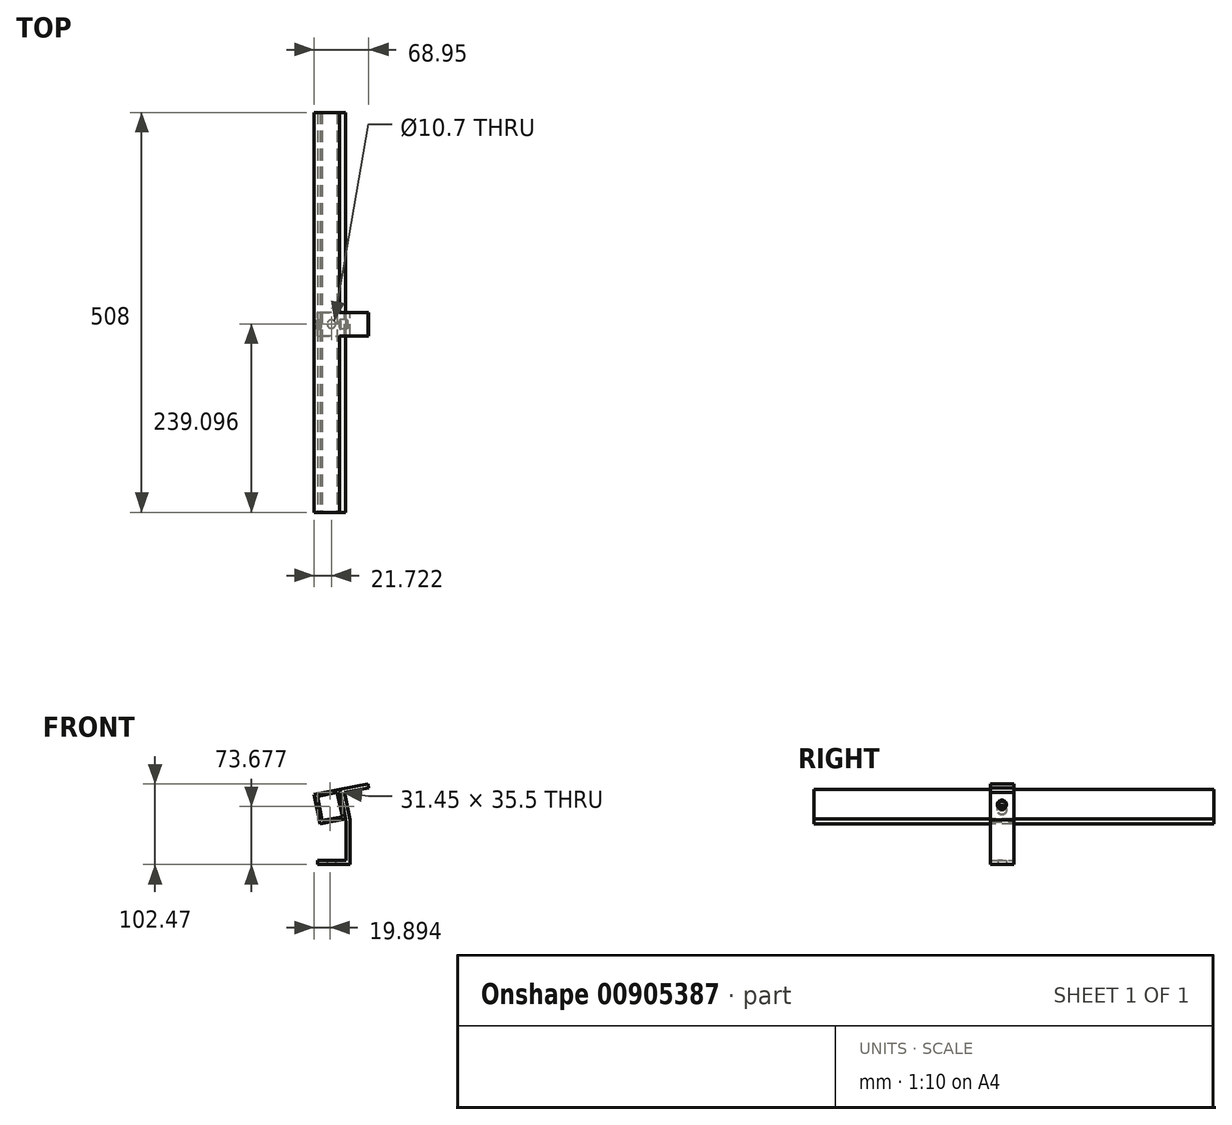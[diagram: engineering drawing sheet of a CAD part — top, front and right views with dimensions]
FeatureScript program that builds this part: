
annotation { "Feature Type Name" : "Feature", "Feature Type Description" : "" }
export const myFeature = defineFeature(function(context is Context, id is Id, definition is map)
    precondition{}
    {
        {
            var Q0;
            Q0=qCreatedBy(makeId("Front.planeOp"),FACE);
            var sketch = newSketch(context, id + "F0", { "sketchPlane" : qUnion([Q0])});
            skLineSegment(sketch, "E0", {"start": v(0, 0) * mm, "end": v(0, 5) * mm});
            skLineSegment(sketch, "E1", {"start": v(0, 5) * mm, "end": v(36, 5) * mm});
            skLineSegment(sketch, "E2", {"start": v(36, 5) * mm, "end": v(36, 54.43) * mm});
            skLineSegment(sketch, "E3", {"start": v(41, 56.52) * mm, "end": v(41, 0) * mm});
            skLineSegment(sketch, "E4", {"start": v(41, 0) * mm, "end": v(0, 0) * mm});
            skLineSegment(sketch, "E5", {"start": v(41, 56.52) * mm, "end": v(34.23, 91.68) * mm});
            skLineSegment(sketch, "E6", {"start": v(34.23, 91.68) * mm, "end": v(64.78, 97.56) * mm});
            skLineSegment(sketch, "E7", {"start": v(64.78, 97.56) * mm, "end": v(63.83, 102.47) * mm});
            skLineSegment(sketch, "E8", {"start": v(63.83, 102.47) * mm, "end": v(28.07, 95.59) * mm});
            skLineSegment(sketch, "E9", {"start": v(28.07, 95.59) * mm, "end": v(36, 54.43) * mm});
            skSolve(sketch);
        }
        {
            var Q0;
            Q0=makeQuery(id+"F0.imprint","IMPRINT",FACE,{"disambiguationData":[TD([[makeQuery(id+"F0.imprint","IMPRINT",EDGE,{"derivedFrom":sQuery(id+"F0.wireOp",EDGE,"E0")}),-1.0]])]});
            extrude(context, id + "F1", {"entities" : qUnion([Q0]), "depth" : 30 * mm, "offsetDistance" : 25.4 * mm});
        }
        {
            var Q0;
            Q0=makeQuery(id+"F1.opExtrude","SWEPT_FACE",FACE,{"disambiguationData":[OSD([sQuery(id+"F0.wireOp",EDGE,"E9")])]});
            var sketch = newSketch(context, id + "F2", { "sketchPlane" : qUnion([Q0])});
            skCircle(sketch, "E10", {"center": v(15.32, 67.61) * mm, "radius": 5.9 * mm});
            skLineSegment(sketch, "E11", {"start": v(15, 88.55) * mm, "end": v(15.64, 46.64) * mm, "construction": true});
            skLineSegment(sketch, "E12", {"start": v(-0.72, 67.6) * mm, "end": v(31.06, 67.6) * mm, "construction": true});
            skPoint(sketch, "E12.startSnap0", {"position": v(0, 67.6) * mm});
            skSolve(sketch);
        }
        {
            var Q0;
            Q0=makeQuery(id+"F2.imprint","IMPRINT",FACE,{"disambiguationData":[TD([[makeQuery(id+"F2.imprint","IMPRINT",EDGE,{"derivedFrom":sQuery(id+"F2.wireOp",EDGE,"E10")}),1.0]])]});
            extrude(context, id + "F3", {"entities" : qUnion([Q0]), "operationType" : NewBodyOperationType.REMOVE, "endBound" : BoundingType.THROUGH_ALL, "oppositeDirection" : true, "depth" : 25.4 * mm, "offsetDistance" : 25.4 * mm});
        }
        {
            var Q0;
            Q0=makeQuery(id+"F1.opExtrude","CAP_FACE",FACE,{"disambiguationData":[OSD([sQuery(id+"F0.wireOp",EDGE,"E0"),sQuery(id+"F0.wireOp",EDGE,"E1"),sQuery(id+"F0.wireOp",EDGE,"E2"),sQuery(id+"F0.wireOp",EDGE,"E3"),sQuery(id+"F0.wireOp",EDGE,"E4"),sQuery(id+"F0.wireOp",EDGE,"E5"),sQuery(id+"F0.wireOp",EDGE,"E6"),sQuery(id+"F0.wireOp",EDGE,"E7"),sQuery(id+"F0.wireOp",EDGE,"E8"),sQuery(id+"F0.wireOp",EDGE,"E9")])],"isStart":true});
            var sketch = newSketch(context, id + "F4", { "sketchPlane" : qUnion([Q0])});
            skLineSegment(sketch, "E13", {"start": v(-28.07, 95.59) * mm, "end": v(4.17, 89.38) * mm});
            skLineSegment(sketch, "E14", {"start": v(4.17, 89.38) * mm, "end": v(-3.12, 51.53) * mm});
            skLineSegment(sketch, "E15", {"start": v(-3.12, 51.53) * mm, "end": v(-35.36, 57.74) * mm});
            skLineSegment(sketch, "E16", {"start": v(-24.86, 91.43) * mm, "end": v(0, 86.64) * mm});
            skLineSegment(sketch, "E17", {"start": v(0, 86.64) * mm, "end": v(-5.91, 55.93) * mm});
            skLineSegment(sketch, "E18", {"start": v(-5.91, 55.93) * mm, "end": v(-31.45, 60.84) * mm});
            skLineSegment(sketch, "E19", {"start": v(-31.45, 60.84) * mm, "end": v(-24.86, 91.43) * mm});
            skSolve(sketch);
        }
        {
            var Q0;
            {var subQ1=sQuery(id+"F4.wireOp",EDGE,"E13");Q0=makeQuery(id+"F4.imprint","IMPRINT",FACE,{"disambiguationData":[TD([[makeQuery(id+"F4.imprint","IMPRINT",EDGE,{"derivedFrom":subQ1}),-1.0]])]});}
            extrude(context, id + "F5", {"entities" : qUnion([Q0]), "operationType" : NewBodyOperationType.ADD, "endBound" : BoundingType.SYMMETRIC, "depth" : 508 * mm, "offsetDistance" : 25.4 * mm});
        }
        {
            var Q0;
            Q0=makeQuery(id+"F1.opExtrude","SWEPT_FACE",FACE,{"disambiguationData":[OSD([sQuery(id+"F0.wireOp",EDGE,"E4")])]});
            var sketch = newSketch(context, id + "F6", { "sketchPlane" : qUnion([Q0])});
            skCircle(sketch, "E20", {"center": v(17.55, 14.9) * mm, "radius": 5.35 * mm});
            skSolve(sketch);
        }
        {
            var Q0;
            Q0=makeQuery(id+"F6.imprint","IMPRINT",FACE,{"disambiguationData":[TD([[makeQuery(id+"F6.imprint","IMPRINT",EDGE,{"derivedFrom":sQuery(id+"F6.wireOp",EDGE,"E20")}),1.0]])]});
            extrude(context, id + "F7", {"entities" : qUnion([Q0]), "operationType" : NewBodyOperationType.REMOVE, "oppositeDirection" : true, "depth" : 25.4 * mm, "offsetDistance" : 25.4 * mm});
        }
        {
            var Q0;
            Q0=makeQuery(id+"F5.boolean.opBoolean","SPLIT",FACE,{"disambiguationData":[TD([makeQuery(id+"F3.boolean.opBoolean","COPY",FACE,{"derivedFrom":makeQuery(id+"F3.opExtrude","SWEPT_FACE",FACE,{"disambiguationData":[OSD([sQuery(id+"F2.wireOp",EDGE,"E10")])]})})])],"derivedFrom":makeQuery(id+"F5.opExtrude","SWEPT_FACE",FACE,{"disambiguationData":[OSD([sQuery(id+"F0.wireOp",EDGE,"E9")])]})});
            extrude(context, id + "F8", {"entities" : qUnion([Q0]), "operationType" : NewBodyOperationType.REMOVE, "endBound" : BoundingType.THROUGH_ALL, "oppositeDirection" : true, "depth" : 25.4 * mm, "offsetDistance" : 25.4 * mm});
        }
    });
